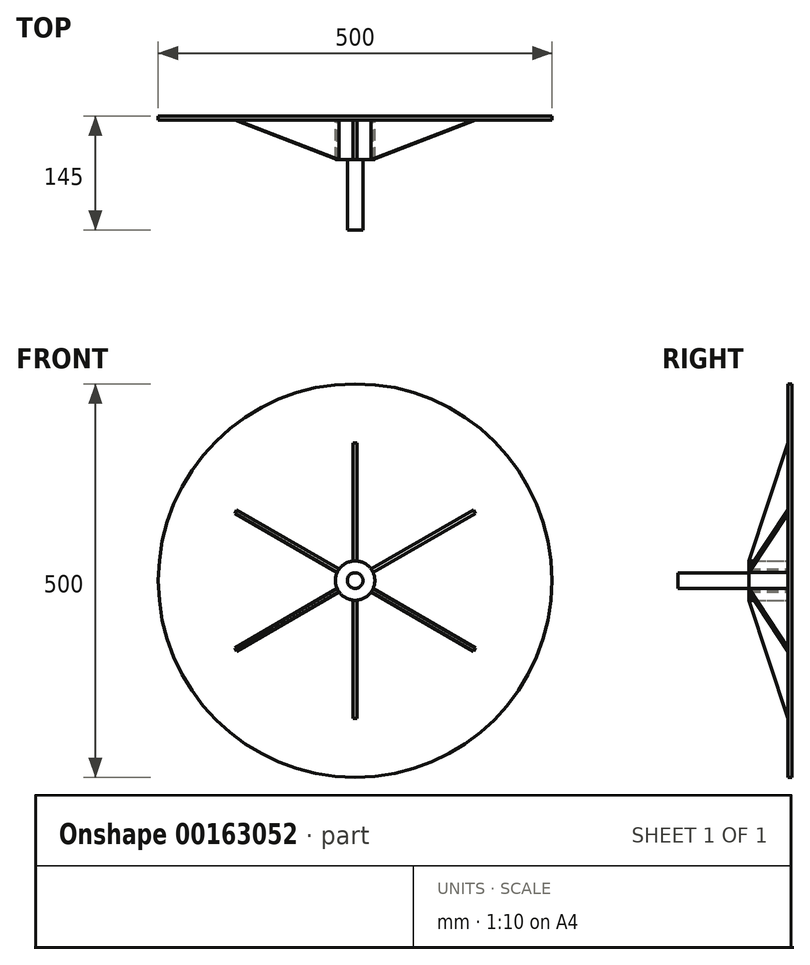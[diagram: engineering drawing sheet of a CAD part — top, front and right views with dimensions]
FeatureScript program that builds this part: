
annotation { "Feature Type Name" : "Feature", "Feature Type Description" : "" }
export const myFeature = defineFeature(function(context is Context, id is Id, definition is map)
    precondition{}
    {
        {
            var Q0;
            Q0=qCreatedBy(makeId("Front.planeOp"),FACE);
            var sketch = newSketch(context, id + "F0", { "sketchPlane" : qUnion([Q0])});
            skCircle(sketch, "E0", {"center": v(0, 0) * mm, "radius": 250 * mm});
            skSolve(sketch);
        }
        {
            var Q0;
            Q0=makeQuery(id+"F0.imprint","IMPRINT",FACE,{"disambiguationData":[TD([[makeQuery(id+"F0.imprint","IMPRINT",EDGE,{"derivedFrom":sQuery(id+"F0.wireOp",EDGE,"E0")}),1.0]])]});
            extrude(context, id + "F1", {"entities" : qUnion([Q0]), "depth" : 5 * mm});
        }
        {
            var Q0;
            Q0=makeQuery(id+"F1.opExtrude","CAP_FACE",FACE,{"disambiguationData":[OSD([sQuery(id+"F0.wireOp",EDGE,"E0")])],"isStart":false});
            var sketch = newSketch(context, id + "F2", { "sketchPlane" : qUnion([Q0])});
            skCircle(sketch, "E1", {"center": v(0, 0) * mm, "radius": 25 * mm});
            skSolve(sketch);
        }
        {
            var Q0;
            Q0 = qSketchRegion(id + "F2", true);
            extrude(context, id + "F3", {"entities" : qUnion([Q0]), "operationType" : NewBodyOperationType.ADD, "depth" : 50 * mm});
        }
        {
            var Q0;
            Q0=makeQuery(id+"F3.opExtrude","CAP_FACE",FACE,{"disambiguationData":[OSD([sQuery(id+"F2.wireOp",EDGE,"E1")])],"isStart":false});
            var sketch = newSketch(context, id + "F4", { "sketchPlane" : qUnion([Q0])});
            skCircle(sketch, "E2", {"center": v(0, 0) * mm, "radius": 10 * mm});
            skSolve(sketch);
        }
        {
            var Q0;
            Q0 = qSketchRegion(id + "F4", true);
            extrude(context, id + "F5", {"entities" : qUnion([Q0]), "operationType" : NewBodyOperationType.ADD, "depth" : 90 * mm});
        }
        {
            var Q0;
            Q0=qCreatedBy(makeId("Right.planeOp"),FACE);
            var sketch = newSketch(context, id + "F6", { "sketchPlane" : qUnion([Q0])});
            skLineSegment(sketch, "E3", {"start": v(-55, 24.94) * mm, "end": v(-5, 24.94) * mm});
            skLineSegment(sketch, "E4", {"start": v(-5, 24.94) * mm, "end": v(-5, 175.07) * mm});
            skLineSegment(sketch, "E5", {"start": v(-5, 175.07) * mm, "end": v(-55, 24.94) * mm});
            skSolve(sketch);
        }
        {
            var Q0;
            Q0=makeQuery(id+"F6.imprint","IMPRINT",FACE,{"disambiguationData":[TD([[makeQuery(id+"F6.imprint","IMPRINT",EDGE,{"derivedFrom":sQuery(id+"F6.wireOp",EDGE,"E3")}),1.0]])]});
            extrude(context, id + "F7", {"entities" : qUnion([Q0]), "endBound" : BoundingType.SYMMETRIC, "depth" : 5 * mm});
        }
        {
            var Q0;
            Q0=makeQuery(id+"F7.opExtrude","SWEPT_BODY",BODY,{"disambiguationData":[OSD([sQuery(id+"F6.wireOp",EDGE,"E3"),sQuery(id+"F6.wireOp",EDGE,"E4"),sQuery(id+"F6.wireOp",EDGE,"E5")])]});
            var Q1;
            Q1=makeQuery(id+"F3.opExtrude","CAP_EDGE",EDGE,{"disambiguationData":[OSD([sQuery(id+"F2.wireOp",EDGE,"E1")])],"isStart":false});
            circularPattern(context, id + "F8", {"operationType" : NewBodyOperationType.ADD, "entities" : qUnion([Q0]), "axis" : qUnion([Q1]), "angle" : 360 * degree, "instanceCount" : 6, "equalSpace" : true});
        }
    });
